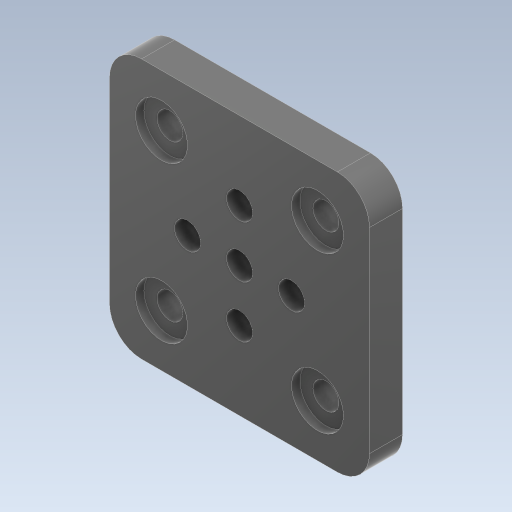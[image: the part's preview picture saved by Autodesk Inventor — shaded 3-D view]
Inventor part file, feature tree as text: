
AUTODESK INVENTOR PART (.ipt)
format: ipt  version: 2023 (Build 270158000, 158)  size: 172,544 bytes
history: native  units: mm
features: extrude x3, sketch x2, mirror x2
ambient origin geometry x8: Origin, YZ Plane, XZ Plane, XY Plane, X Axis, Y Axis, Z Axis, Center Point
bodies: Solid1 (feature_tree)
feature tree (7):
  sketch  "Sketch1"  dims[d0=50.0mm d1=50.0mm]
  extrude  "Extrusion1"  Depth=50.0mm
  sketch  "Sketch2"  dims[d2=5.02mm d3=5.02mm d4=40.0mm d6=360.0deg d8=10.0mm d9=6.17mm d14=6.35mm d15=0.0mm d18=10.0mm d19=5.0mm d20=15.0mm d21=15.0mm d22=1.625mm d23=0.0mm d24=0.0mm d25=0.0mm d16=0.5mm d17=0.872665mm]
  extrude  "Extrusion3"  Depth=1.625mm
  extrude  "Extrusion4"  Depth=1.625mm TaperAngle=360.0deg
  mirror  "Mirror1"
  mirror  "Mirror2"
